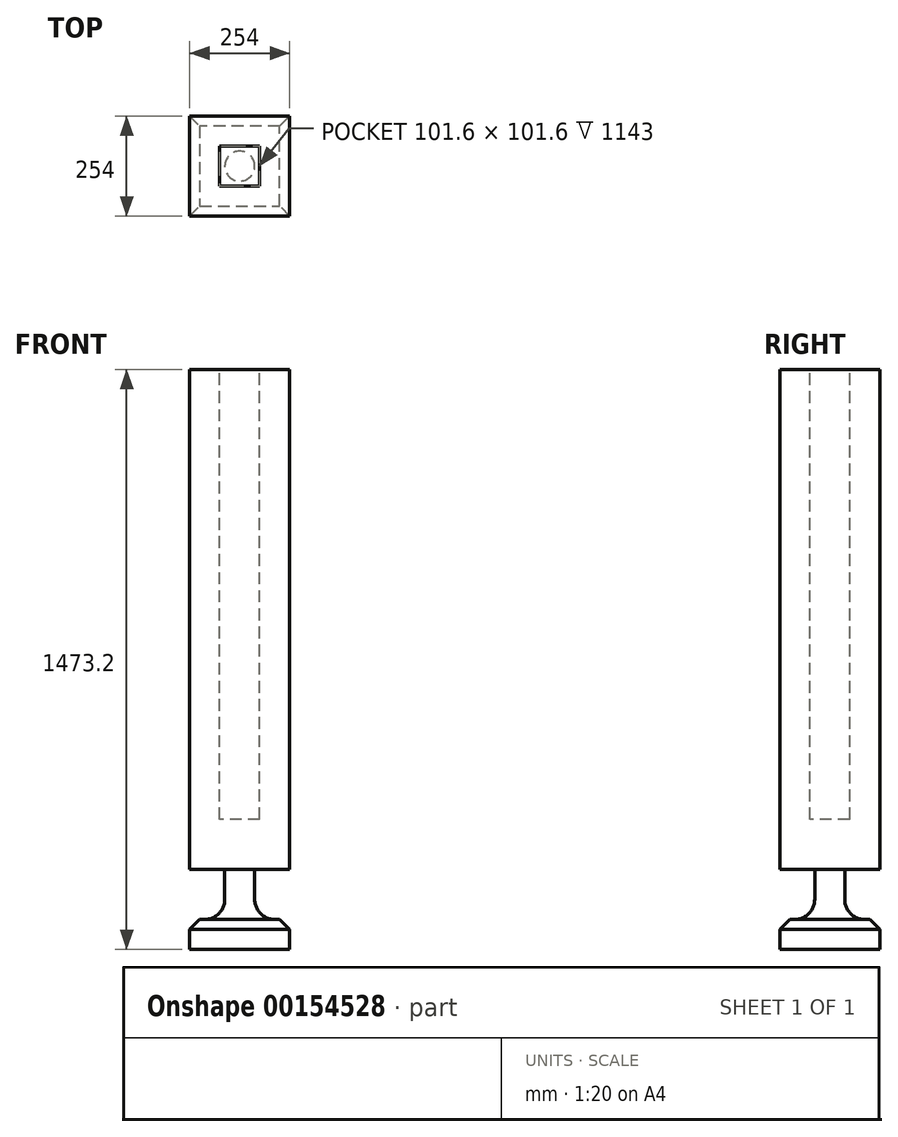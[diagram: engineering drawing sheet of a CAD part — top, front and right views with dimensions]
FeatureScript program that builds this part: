
annotation { "Feature Type Name" : "Feature", "Feature Type Description" : "" }
export const myFeature = defineFeature(function(context is Context, id is Id, definition is map)
    precondition{}
    {
        {
            var Q0;
            Q0=qCreatedBy(makeId("Top.planeOp"),FACE);
            var sketch = newSketch(context, id + "F0", { "sketchPlane" : qUnion([Q0])});
            skLineSegment(sketch, "E0.bottom", {"start": v(127, 127) * mm, "end": v(-127, 127) * mm});
            skLineSegment(sketch, "E0.top", {"start": v(127, -127) * mm, "end": v(-127, -127) * mm});
            skLineSegment(sketch, "E0.left", {"start": v(127, 127) * mm, "end": v(127, -127) * mm});
            skLineSegment(sketch, "E0.right", {"start": v(-127, 127) * mm, "end": v(-127, -127) * mm});
            skPoint(sketch, "E0.middle", {"position": v(0, 0) * mm});
            skCircle(sketch, "E1", {"center": v(0, 0) * mm, "radius": 38.1 * mm});
            skSolve(sketch);
        }
        {
            var Q0;
            Q0=makeQuery(id+"F0.imprint","IMPRINT",FACE,{"disambiguationData":[TD([[makeQuery(id+"F0.imprint","IMPRINT",EDGE,{"derivedFrom":sQuery(id+"F0.wireOp",EDGE,"E0.bottom")}),1.0]])]});
            var Q1;
            Q1=makeQuery(id+"F0.imprint","IMPRINT",FACE,{"disambiguationData":[TD([[makeQuery(id+"F0.imprint","IMPRINT",EDGE,{"derivedFrom":sQuery(id+"F0.wireOp",EDGE,"E1")}),1.0]])]});
            extrude(context, id + "F1", {"entities" : qUnion([Q0, Q1]), "depth" : 76.2 * mm});
        }
        {
            var Q0;
            Q0=makeQuery(id+"F0.imprint","IMPRINT",FACE,{"disambiguationData":[TD([[makeQuery(id+"F0.imprint","IMPRINT",EDGE,{"derivedFrom":sQuery(id+"F0.wireOp",EDGE,"E1")}),1.0]])]});
            extrude(context, id + "F2", {"entities" : qUnion([Q0]), "operationType" : NewBodyOperationType.ADD, "depth" : 203.2 * mm});
        }
        {
            var Q0;
            Q0=makeQuery(id+"F2.opExtrude","CAP_FACE",FACE,{"disambiguationData":[OSD([sQuery(id+"F0.wireOp",EDGE,"E1")])],"isStart":false});
            var sketch = newSketch(context, id + "F3", { "sketchPlane" : qUnion([Q0])});
            skLineSegment(sketch, "E2.bottom", {"start": v(127, -127) * mm, "end": v(-127, -127) * mm});
            skLineSegment(sketch, "E2.top", {"start": v(127, 127) * mm, "end": v(-127, 127) * mm});
            skLineSegment(sketch, "E2.left", {"start": v(127, -127) * mm, "end": v(127, 127) * mm});
            skLineSegment(sketch, "E2.right", {"start": v(-127, -127) * mm, "end": v(-127, 127) * mm});
            skPoint(sketch, "E2.middle", {"position": v(0, 0) * mm});
            skSolve(sketch);
        }
        {
            var Q0;
            Q0=makeQuery(id+"F3.imprint","IMPRINT",FACE,{"disambiguationData":[TD([[makeQuery(id+"F3.imprint","IMPRINT",EDGE,{"derivedFrom":sQuery(id+"F3.wireOp",EDGE,"E2.bottom")}),-1.0]])]});
            var Q1;
            Q1=makeQuery(id+"F3.imprint","IMPRINT",FACE,{"disambiguationData":[TD([[makeQuery(id+"F3.imprint","IMPRINT",EDGE,{"derivedFrom":makeQuery(id+"F2.opExtrude","CAP_EDGE",EDGE,{"disambiguationData":[OSD([sQuery(id+"F0.wireOp",EDGE,"E1")])],"isStart":false})}),1.0]])]});
            extrude(context, id + "F4", {"entities" : qUnion([Q0, Q1]), "operationType" : NewBodyOperationType.ADD, "depth" : 1270 * mm});
        }
        {
            var Q0;
            Q0=makeQuery(id+"F4.opExtrude","CAP_FACE",FACE,{"disambiguationData":[OSD([sQuery(id+"F3.wireOp",EDGE,"E2.bottom"),sQuery(id+"F3.wireOp",EDGE,"E2.top"),sQuery(id+"F3.wireOp",EDGE,"E2.left"),sQuery(id+"F3.wireOp",EDGE,"E2.right")])],"isStart":false});
            var sketch = newSketch(context, id + "F5", { "sketchPlane" : qUnion([Q0])});
            skLineSegment(sketch, "E3.bottom", {"start": v(50.8, 50.8) * mm, "end": v(-50.8, 50.8) * mm});
            skLineSegment(sketch, "E3.top", {"start": v(50.8, -50.8) * mm, "end": v(-50.8, -50.8) * mm});
            skLineSegment(sketch, "E3.left", {"start": v(50.8, 50.8) * mm, "end": v(50.8, -50.8) * mm});
            skLineSegment(sketch, "E3.right", {"start": v(-50.8, 50.8) * mm, "end": v(-50.8, -50.8) * mm});
            skPoint(sketch, "E3.middle", {"position": v(0, 0) * mm});
            skCircle(sketch, "E4", {"center": v(0, 0) * mm, "radius": 50.8 * mm});
            skSolve(sketch);
        }
        {
            var Q0;
            {var subQ0=sQuery(id+"F5.wireOp",EDGE,"E3.left");var subQ1=sQuery(id+"F5.wireOp",EDGE,"E3.bottom");var subQ2=makeQuery(id+"F5.imprint","INTERSECT",VERTEX,{"derivedFrom":[subQ1,subQ0]});Q0=makeQuery(id+"F5.imprint","IMPRINT",FACE,{"disambiguationData":[TD([[makeQuery(id+"F5.imprint","IMPRINT",EDGE,{"disambiguationData":[TD([[subQ2,-1.0]])],"derivedFrom":subQ1}),1.0]])]});}
            var Q1;
            {var subQ0=sQuery(id+"F5.wireOp",EDGE,"E3.left");var subQ1=sQuery(id+"F5.wireOp",EDGE,"E3.top");var subQ2=makeQuery(id+"F5.imprint","INTERSECT",VERTEX,{"derivedFrom":[subQ1,subQ0]});Q1=makeQuery(id+"F5.imprint","IMPRINT",FACE,{"disambiguationData":[TD([[makeQuery(id+"F5.imprint","IMPRINT",EDGE,{"disambiguationData":[TD([[subQ2,-1.0]])],"derivedFrom":subQ1}),-1.0]])]});}
            var Q2;
            {var subQ0=sQuery(id+"F5.wireOp",EDGE,"E3.right");var subQ1=sQuery(id+"F5.wireOp",EDGE,"E3.top");var subQ2=makeQuery(id+"F5.imprint","INTERSECT",VERTEX,{"derivedFrom":[subQ1,subQ0]});Q2=makeQuery(id+"F5.imprint","IMPRINT",FACE,{"disambiguationData":[TD([[makeQuery(id+"F5.imprint","IMPRINT",EDGE,{"disambiguationData":[TD([[subQ2,1.0]])],"derivedFrom":subQ1}),-1.0]])]});}
            var Q3;
            {var subQ0=sQuery(id+"F5.wireOp",EDGE,"E3.right");var subQ1=sQuery(id+"F5.wireOp",EDGE,"E3.bottom");var subQ2=makeQuery(id+"F5.imprint","INTERSECT",VERTEX,{"derivedFrom":[subQ1,subQ0]});Q3=makeQuery(id+"F5.imprint","IMPRINT",FACE,{"disambiguationData":[TD([[makeQuery(id+"F5.imprint","IMPRINT",EDGE,{"disambiguationData":[TD([[subQ2,1.0]])],"derivedFrom":subQ1}),1.0]])]});}
            var Q4;
            {var subQ0=sQuery(id+"F5.wireOp",EDGE,"E4");var subQ1=makeQuery(id+"F5.imprint","INTERSECT",VERTEX,{"derivedFrom":[sQuery(id+"F5.wireOp",EDGE,"E3.bottom"),subQ0]});Q4=makeQuery(id+"F5.imprint","IMPRINT",FACE,{"disambiguationData":[TD([[makeQuery(id+"F5.imprint","IMPRINT",EDGE,{"disambiguationData":[TD([[subQ1,1.0]])],"derivedFrom":subQ0}),1.0]])]});}
            extrude(context, id + "F6", {"entities" : qUnion([Q0, Q1, Q2, Q3, Q4]), "operationType" : NewBodyOperationType.REMOVE, "oppositeDirection" : true, "depth" : 1143 * mm});
        }
        {
            var Q0;
            Q0=makeQuery(id+"F2.boolean.opBoolean","INTERSECT",EDGE,{"derivedFrom":[makeQuery(id+"F1.opExtrude","CAP_FACE",FACE,{"disambiguationData":[OSD([sQuery(id+"F0.wireOp",EDGE,"E0.bottom"),sQuery(id+"F0.wireOp",EDGE,"E0.top"),sQuery(id+"F0.wireOp",EDGE,"E0.left"),sQuery(id+"F0.wireOp",EDGE,"E0.right")])],"isStart":false}),makeQuery(id+"F2.opExtrude","SWEPT_FACE",FACE,{"disambiguationData":[OSD([sQuery(id+"F0.wireOp",EDGE,"E1")])]})]});
            var Q1;
            Q1=makeQuery(id+"F2.opExtrude","CAP_EDGE",EDGE,{"disambiguationData":[OSD([sQuery(id+"F0.wireOp",EDGE,"E1")])],"isStart":false});
            fillet(context, id + "F7", {"entities" : qUnion([Q0, Q1]), "radius" : 50.8 * mm, "tangentPropagation" : true, "allowEdgeOverflow" : false});
        }
        {
            var Q0;
            Q0=makeQuery(id+"F1.opExtrude","CAP_EDGE",EDGE,{"disambiguationData":[OSD([sQuery(id+"F0.wireOp",EDGE,"E0.top")])],"isStart":false});
            var Q1;
            Q1=makeQuery(id+"F1.opExtrude","CAP_EDGE",EDGE,{"disambiguationData":[OSD([sQuery(id+"F0.wireOp",EDGE,"E0.left")])],"isStart":false});
            var Q2;
            Q2=makeQuery(id+"F1.opExtrude","CAP_EDGE",EDGE,{"disambiguationData":[OSD([sQuery(id+"F0.wireOp",EDGE,"E0.bottom")])],"isStart":false});
            var Q3;
            Q3=makeQuery(id+"F1.opExtrude","CAP_EDGE",EDGE,{"disambiguationData":[OSD([sQuery(id+"F0.wireOp",EDGE,"E0.right")])],"isStart":false});
            chamfer(context, id + "F8", {"entities" : qUnion([Q0, Q1, Q2, Q3]), "width" : 25.4 * mm, "tangentPropagation" : true});
        }
    });
